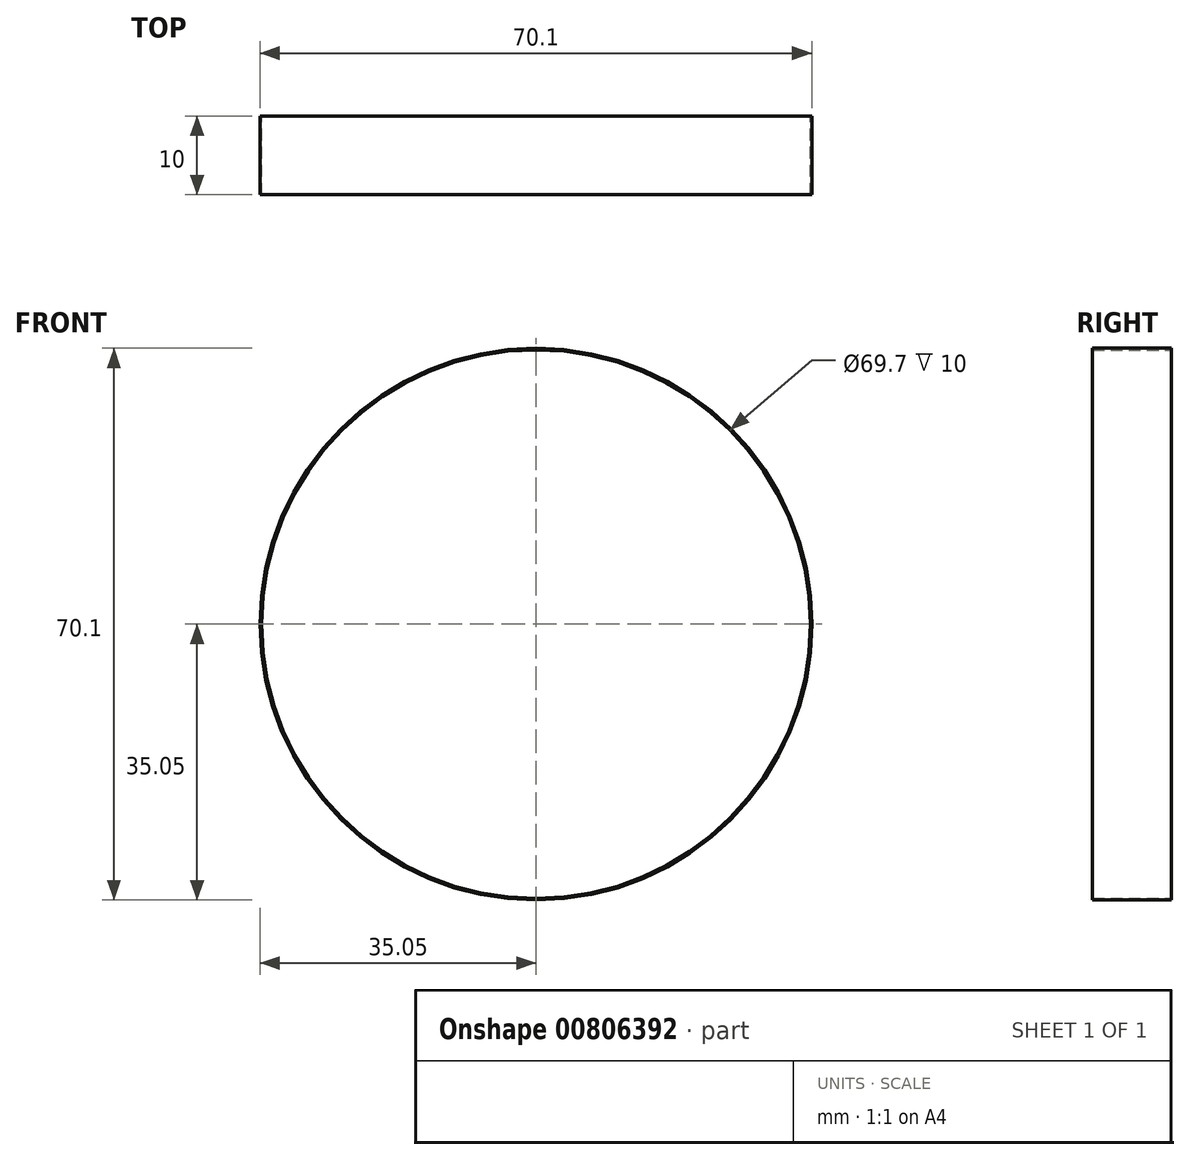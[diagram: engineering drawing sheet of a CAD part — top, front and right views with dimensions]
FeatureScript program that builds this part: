
annotation { "Feature Type Name" : "Feature", "Feature Type Description" : "" }
export const myFeature = defineFeature(function(context is Context, id is Id, definition is map)
    precondition{}
    {
        {
            var Q0;
            Q0=qCreatedBy(makeId("Front.planeOp"),FACE);
            var sketch = newSketch(context, id + "F0", { "sketchPlane" : qUnion([Q0])});
            skCircle(sketch, "E0", {"center": v(0, 0) * mm, "radius": 35.05 * mm});
            skCircle(sketch, "E1", {"center": v(0, 0) * mm, "radius": 34.85 * mm});
            skSolve(sketch);
        }
        {
            var Q0;
            Q0=makeQuery(id+"F0.imprint","IMPRINT",FACE,{"disambiguationData":[TD([[makeQuery(id+"F0.imprint","IMPRINT",EDGE,{"derivedFrom":sQuery(id+"F0.wireOp",EDGE,"E0")}),1.0]])]});
            extrude(context, id + "F1", {"entities" : qUnion([Q0]), "depth" : 10 * mm, "offsetDistance" : 25 * mm});
        }
    });
